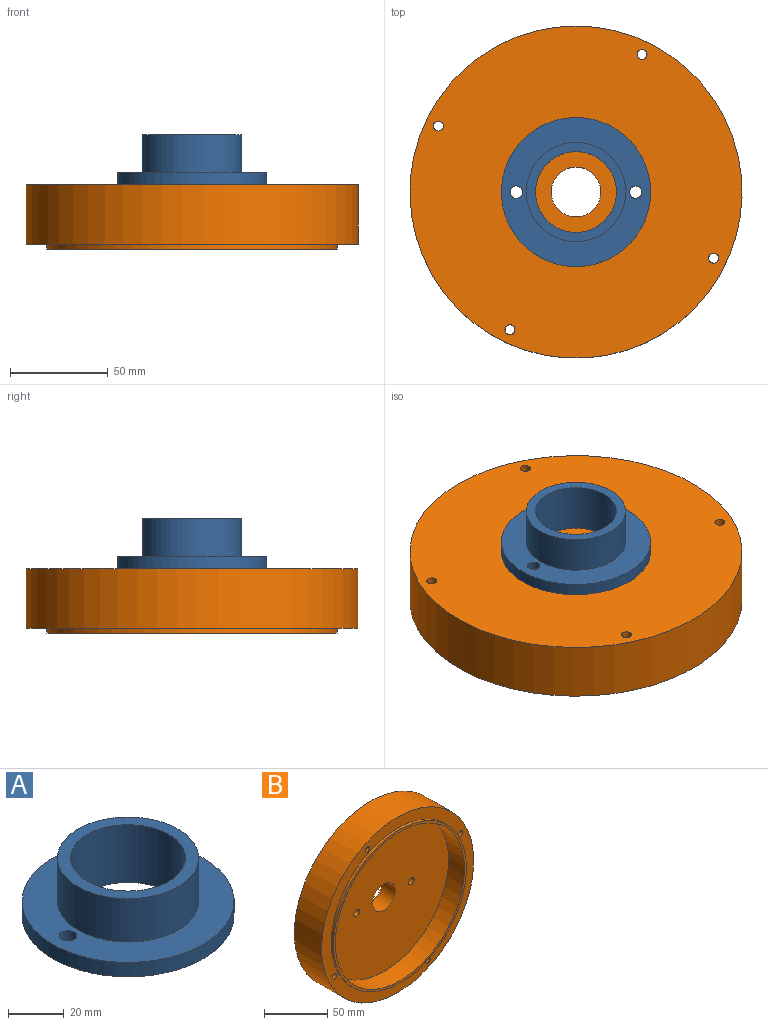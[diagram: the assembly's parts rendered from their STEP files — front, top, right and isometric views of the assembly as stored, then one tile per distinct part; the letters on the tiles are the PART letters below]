
ASSEMBLY  parts=2 mates=1
PART A: 8 faces, bbox 76.2x76.2x25.4 mm
  f0: cylinder r=20.64mm len=41.28mm, axis (0,0,-1), area 3293.6mm2, adj f5,f7
  f1: cylinder r=3.17mm len=6.35mm, axis (0,0,-1), area 126.7mm2, adj f4,f5
  f2: cylinder r=3.17mm len=6.35mm, axis (0,0,-1), area 126.7mm2, adj f4,f5
  f3: cylinder r=38.1mm len=76.2mm, axis (0,0,-1), area 1520.1mm2, adj f4,f5
  f4: plane 76.2x76.2mm, normal (0,0,1), area 2470.2mm2, adj f1,f2,f3,f6
  f5: plane 76.2x76.2mm, normal (0,0,-1), area 3159mm2, adj f0,f1,f2,f3
  f6: cylinder r=25.4mm len=50.8mm, axis (0,0,-1), area 3040.2mm2, adj f4,f7
  f7: plane 50.8x50.8mm, normal (0,0,1), area 688.8mm2, adj f0,f6
PART B: 14 faces, bbox 169.7x33x169.7 mm
  f0: cylinder r=3.17mm len=15.24mm, axis (0,1,0), area 304mm2, adj f3,f4
  f1: cylinder r=3.17mm len=15.24mm, axis (0,1,0), area 304mm2, adj f3,f4
  f2: cylinder r=12.7mm len=25.4mm, axis (0,1,0), area 1216.1mm2, adj f3,f4
  f3: plane 144.06x144.06mm, normal (0,-1,0), area 15728.5mm2, adj f0,f1,f2,f11
  f4: plane 169.67x169.67mm, normal (0,1,0), area 21959.4mm2, adj f0,f1,f2,f5,f6,f7,f8,f9
  f5: cylinder r=2.54mm len=30.48mm, axis (0,1,0), area 486.4mm2, adj f4,f10
  f6: cylinder r=2.54mm len=30.48mm, axis (0,1,0), area 486.4mm2, adj f4,f10
  f7: cylinder r=2.54mm len=30.48mm, axis (0,1,0), area 486.4mm2, adj f4,f10
  f8: cylinder r=2.54mm len=30.48mm, axis (0,1,0), area 486.4mm2, adj f4,f10
  f9: cylinder r=84.84mm len=169.67mm, axis (0,1,0), area 16247.1mm2, adj f4,f10
  f10: plane 169.67x169.67mm, normal (0,-1,0), area 5247.9mm2, adj f5,f6,f7,f8,f9,f12
  f11: cylinder r=72.03mm len=144.06mm, axis (0,1,0), area 8046.6mm2, adj f3,f13
  f12: cylinder r=74.17mm len=148.34mm, axis (0,1,0), area 1183.7mm2, adj f10,f13
  f13: plane 148.34x148.34mm, normal (0,-1,0), area 983mm2, adj f11,f12
PLACE A t=(51.43,-179.3,17.46)mm
PLACE B rot(axis=(1,0,0),90deg) t=(51.43,-179.3,17.46)mm
MATE fastened B.f1 <-> A.f2  axis (0,0,1) through (81.91,-179.3,17.46)mm
